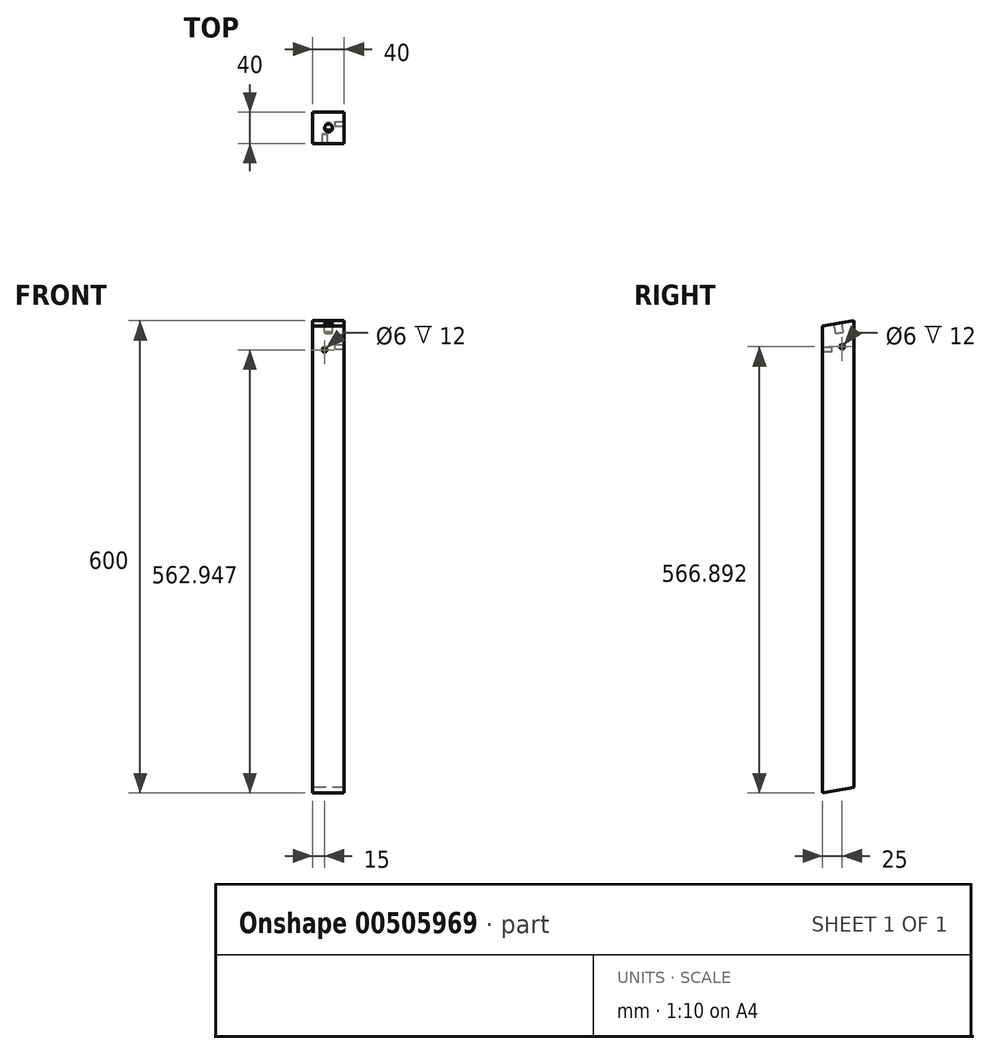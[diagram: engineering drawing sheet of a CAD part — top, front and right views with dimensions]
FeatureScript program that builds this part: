
annotation { "Feature Type Name" : "Feature", "Feature Type Description" : "" }
export const myFeature = defineFeature(function(context is Context, id is Id, definition is map)
    precondition{}
    {
        {
            var Q0;
            Q0=qCreatedBy(makeId("Top.planeOp"),FACE);
            var sketch = newSketch(context, id + "F0", { "sketchPlane" : qUnion([Q0])});
            skLineSegment(sketch, "E0.bottom", {"start": v(0, 0) * mm, "end": v(40, 0) * mm});
            skLineSegment(sketch, "E0.top", {"start": v(0, 40) * mm, "end": v(40, 40) * mm});
            skLineSegment(sketch, "E0.left", {"start": v(0, 0) * mm, "end": v(0, 40) * mm});
            skLineSegment(sketch, "E0.right", {"start": v(40, 0) * mm, "end": v(40, 40) * mm});
            skSolve(sketch);
        }
        {
            var Q0;
            Q0=makeQuery(id+"F0.imprint","IMPRINT",FACE,{"disambiguationData":[TD([[makeQuery(id+"F0.imprint","IMPRINT",EDGE,{"derivedFrom":sQuery(id+"F0.wireOp",EDGE,"E0.bottom")}),1.0]])]});
            extrude(context, id + "F1", {"entities" : qUnion([Q0]), "depth" : 600 * mm, "offsetDistance" : 25 * mm});
        }
        {
            var Q0;
            Q0=makeQuery(id+"F1.opExtrude","CAP_EDGE",EDGE,{"disambiguationData":[OSD([sQuery(id+"F0.wireOp",EDGE,"E0.bottom")])],"isStart":false});
            chamfer(context, id + "F2", {"entities" : qUnion([Q0]), "chamferType" : ChamferType.OFFSET_ANGLE, "width" : 40 * mm, "oppositeDirection" : false, "angle" : 10 * degree, "tangentPropagation" : true});
        }
        {
            var Q0;
            Q0=makeQuery(id+"F1.opExtrude","CAP_EDGE",EDGE,{"disambiguationData":[OSD([sQuery(id+"F0.wireOp",EDGE,"E0.top")])],"isStart":true});
            chamfer(context, id + "F3", {"entities" : qUnion([Q0]), "chamferType" : ChamferType.OFFSET_ANGLE, "width" : 40 * mm, "oppositeDirection" : false, "angle" : 10 * degree, "tangentPropagation" : true});
        }
        {
            var Q0;
            Q0=makeQuery(id+"F1.opExtrude","SWEPT_FACE",FACE,{"disambiguationData":[OSD([sQuery(id+"F0.wireOp",EDGE,"E0.bottom")])]});
            var sketch = newSketch(context, id + "F4", { "sketchPlane" : qUnion([Q0])});
            skCircle(sketch, "E1", {"center": v(15, 562.95) * mm, "radius": 3 * mm});
            skSolve(sketch);
        }
        {
            var Q0;
            Q0=makeQuery(id+"F1.opExtrude","SWEPT_FACE",FACE,{"disambiguationData":[OSD([sQuery(id+"F0.wireOp",EDGE,"E0.right")])]});
            var sketch = newSketch(context, id + "F5", { "sketchPlane" : qUnion([Q0])});
            skCircle(sketch, "E2", {"center": v(25, 566.9) * mm, "radius": 3 * mm});
            skSolve(sketch);
        }
        {
            var Q0;
            Q0=makeQuery(id+"F4.imprint","IMPRINT",FACE,{"disambiguationData":[TD([[makeQuery(id+"F4.imprint","IMPRINT",EDGE,{"derivedFrom":sQuery(id+"F4.wireOp",EDGE,"E1")}),1.0]])]});
            extrude(context, id + "F6", {"entities" : qUnion([Q0]), "operationType" : NewBodyOperationType.REMOVE, "oppositeDirection" : true, "depth" : 12 * mm, "offsetDistance" : 25 * mm});
        }
        {
            var Q0;
            Q0=makeQuery(id+"F5.imprint","IMPRINT",FACE,{"disambiguationData":[TD([[makeQuery(id+"F5.imprint","IMPRINT",EDGE,{"derivedFrom":sQuery(id+"F5.wireOp",EDGE,"E2")}),1.0]])]});
            extrude(context, id + "F7", {"entities" : qUnion([Q0]), "operationType" : NewBodyOperationType.REMOVE, "oppositeDirection" : true, "depth" : 12 * mm, "offsetDistance" : 25 * mm});
        }
        {
            var Q0;
            Q0=makeQuery(id+"F2.opChamfer","BLEND_FACE",FACE,{"disambiguationData":[OSD([sQuery(id+"F0.wireOp",EDGE,"E0.bottom")])]});
            var sketch = newSketch(context, id + "F8", { "sketchPlane" : qUnion([Q0])});
            skCircle(sketch, "E3", {"center": v(20, 122.96) * mm, "radius": 5 * mm});
            skSolve(sketch);
        }
        {
            var Q0;
            Q0=makeQuery(id+"F8.imprint","IMPRINT",FACE,{"disambiguationData":[TD([[makeQuery(id+"F8.imprint","IMPRINT",EDGE,{"derivedFrom":sQuery(id+"F8.wireOp",EDGE,"E3")}),1.0]])]});
            extrude(context, id + "F9", {"entities" : qUnion([Q0]), "operationType" : NewBodyOperationType.REMOVE, "oppositeDirection" : true, "depth" : 12 * mm, "offsetDistance" : 25 * mm});
        }
    });
